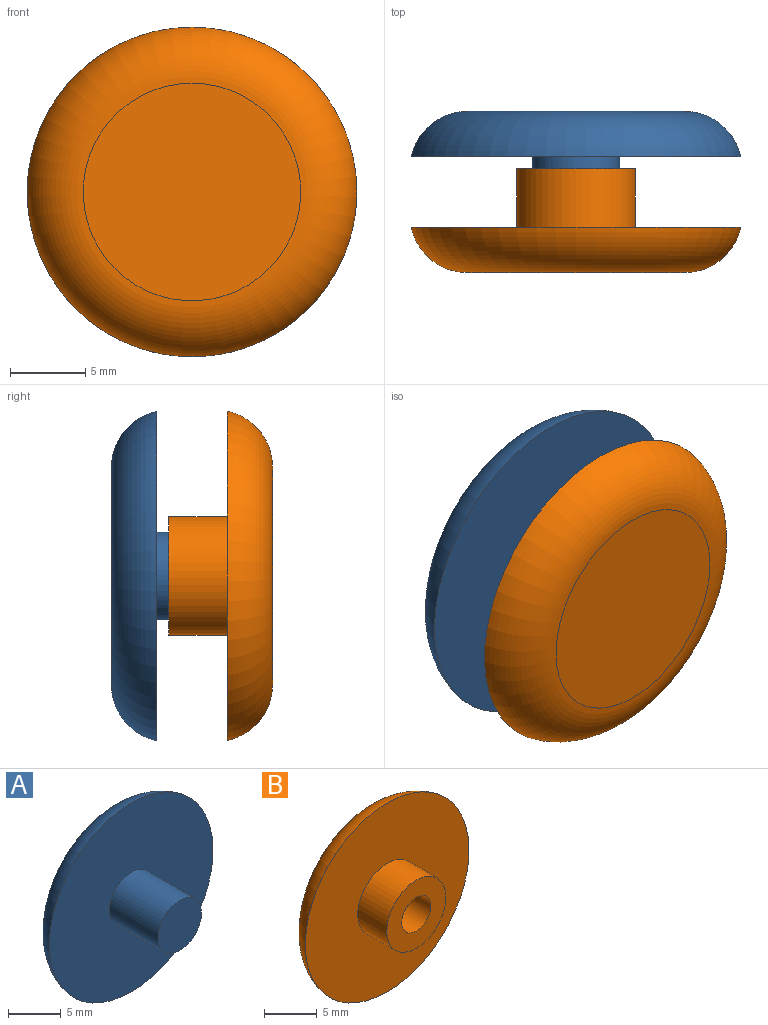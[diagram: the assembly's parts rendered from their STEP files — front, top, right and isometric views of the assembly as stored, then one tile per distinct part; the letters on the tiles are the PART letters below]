
ASSEMBLY  parts=2 mates=1
PART A: 5 faces, bbox 23.9x9.5x23.9 mm
  f0: plane 21.9x21.9mm, normal (0,-1,0), area 350mm2, adj f2,f4
  f1: plane 14.45x14.45mm, normal (0,1,0), area 164.1mm2, adj f4
  f2: cylinder r=2.92mm len=6.5mm, axis (0,1,0), area 119.1mm2, adj f0,f3
  f3: plane 5.83x5.83mm, normal (0,-1,0), area 26.7mm2, adj f2
  f4: torus R=7.23mm, axis (0,1,0), area 306.5mm2, adj f0,f1
PART B: 7 faces, bbox 23.9x6.9x23.9 mm
  f0: plane 21.9x21.9mm, normal (0,-1,0), area 327.7mm2, adj f2,f6
  f1: plane 14.45x14.45mm, normal (0,1,0), area 164.1mm2, adj f6
  f2: cylinder r=3.95mm len=7.9mm, axis (0,1,0), area 96.8mm2, adj f0,f3
  f3: plane 7.9x7.9mm, normal (0,-1,0), area 37.1mm2, adj f2,f5
  f4: plane 3.9x3.9mm, normal (0,-1,0), area 11.9mm2, adj f5
  f5: cylinder r=1.95mm len=4.9mm, axis (0,1,0), area 60mm2, adj f3,f4
  f6: torus R=7.23mm, axis (0,1,0), area 306.5mm2, adj f0,f1
PLACE A t=(0,-0.15,0)mm
PLACE B rot(axis=(1,0,0),180deg) t=(0,-10.85,0)mm
MATE fastened B.f2 <-> A.f2  axis (0,-1,0) through (0,-6.4,0)mm
